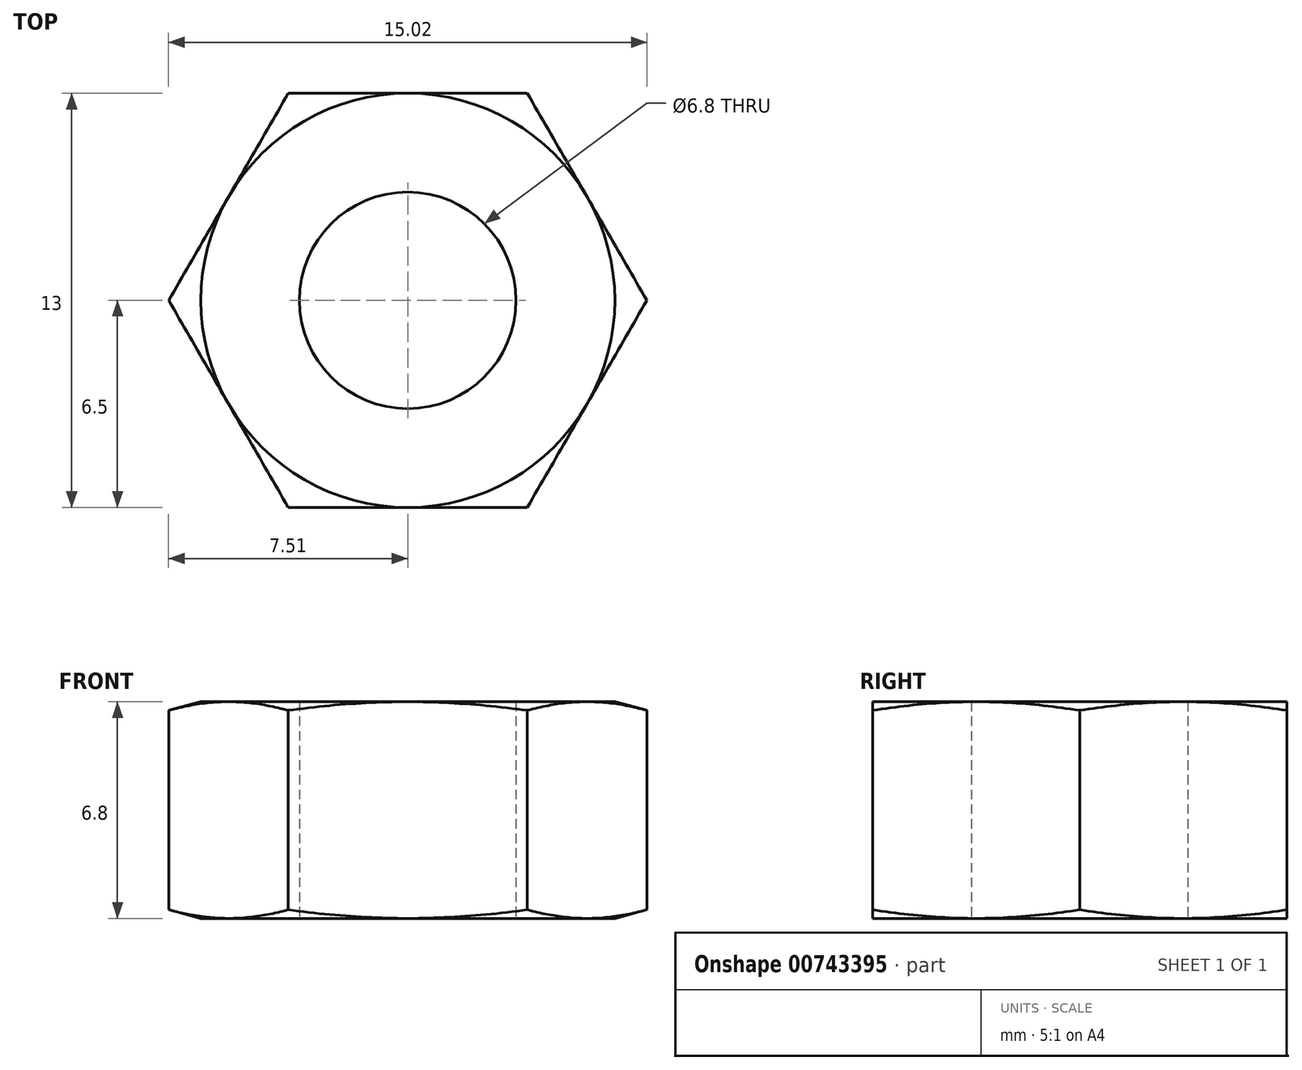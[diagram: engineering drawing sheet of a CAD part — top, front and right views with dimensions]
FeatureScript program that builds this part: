
annotation { "Feature Type Name" : "Feature", "Feature Type Description" : "" }
export const myFeature = defineFeature(function(context is Context, id is Id, definition is map)
    precondition{}
    {
        {
            var Q0;
            Q0=qCreatedBy(makeId("Top.planeOp"),FACE);
            var sketch = newSketch(context, id + "F0", { "sketchPlane" : qUnion([Q0])});
            skCircle(sketch, "E0.cCircle", {"center": v(0, 0) * mm, "radius": 6.5 * mm, "construction": true});
            skLineSegment(sketch, "E0.0", {"start": v(3.75, -6.5) * mm, "end": v(-3.75, -6.5) * mm});
            skLineSegment(sketch, "E0.1", {"start": v(-3.75, -6.5) * mm, "end": v(-7.5, 0) * mm});
            skLineSegment(sketch, "E0.2", {"start": v(-7.5, 0) * mm, "end": v(-3.75, 6.5) * mm});
            skLineSegment(sketch, "E0.3", {"start": v(-3.75, 6.5) * mm, "end": v(3.75, 6.5) * mm});
            skLineSegment(sketch, "E0.4", {"start": v(3.75, 6.5) * mm, "end": v(7.5, 0) * mm});
            skLineSegment(sketch, "E0.5", {"start": v(7.5, 0) * mm, "end": v(3.75, -6.5) * mm});
            skPoint(sketch, "E0.0.midPoint", {"position": v(0, -6.5) * mm});
            skCircle(sketch, "E1", {"center": v(0, 0) * mm, "radius": 3.4 * mm});
            skSolve(sketch);
        }
        {
            var Q0;
            Q0 = qSketchRegion(id + "F0", true);
            extrude(context, id + "F1", {"entities" : qUnion([Q0]), "depth" : 6.8 * mm, "offsetDistance" : 25 * mm});
        }
        {
            var Q0;
            Q0=qCreatedBy(makeId("Front.planeOp"),FACE);
            var sketch = newSketch(context, id + "F2", { "sketchPlane" : qUnion([Q0])});
            skLineSegment(sketch, "E2", {"start": v(-6.5, 0) * mm, "end": v(-7.5, 0.27) * mm});
            skLineSegment(sketch, "E3", {"start": v(-7.5, 0.27) * mm, "end": v(-7.5, 0) * mm});
            skLineSegment(sketch, "E4", {"start": v(-7.5, 0) * mm, "end": v(-6.5, 0) * mm});
            skLineSegment(sketch, "E5", {"start": v(-7.5, 6.53) * mm, "end": v(-6.5, 6.8) * mm});
            skLineSegment(sketch, "E6", {"start": v(-6.5, 6.8) * mm, "end": v(-7.5, 6.8) * mm});
            skLineSegment(sketch, "E7", {"start": v(-7.5, 6.8) * mm, "end": v(-7.5, 6.53) * mm});
            skLineSegment(sketch, "E8", {"start": v(0, -2.48) * mm, "end": v(0, 13.77) * mm, "construction": true});
            skSolve(sketch);
        }
        {
            var Q0;
            Q0 = qSketchRegion(id + "F2", true);
            var Q1;
            Q1=sQuery(id+"F2.wireOp",EDGE,"E8");
            revolve(context, id + "F3", {"operationType" : NewBodyOperationType.REMOVE, "surfaceOperationType" : NewSurfaceOperationType.NEW, "entities" : qUnion([Q0]), "axis" : qUnion([Q1]), "revolveType" : RevolveType.FULL, "oppositeDirection" : true});
        }
    });
